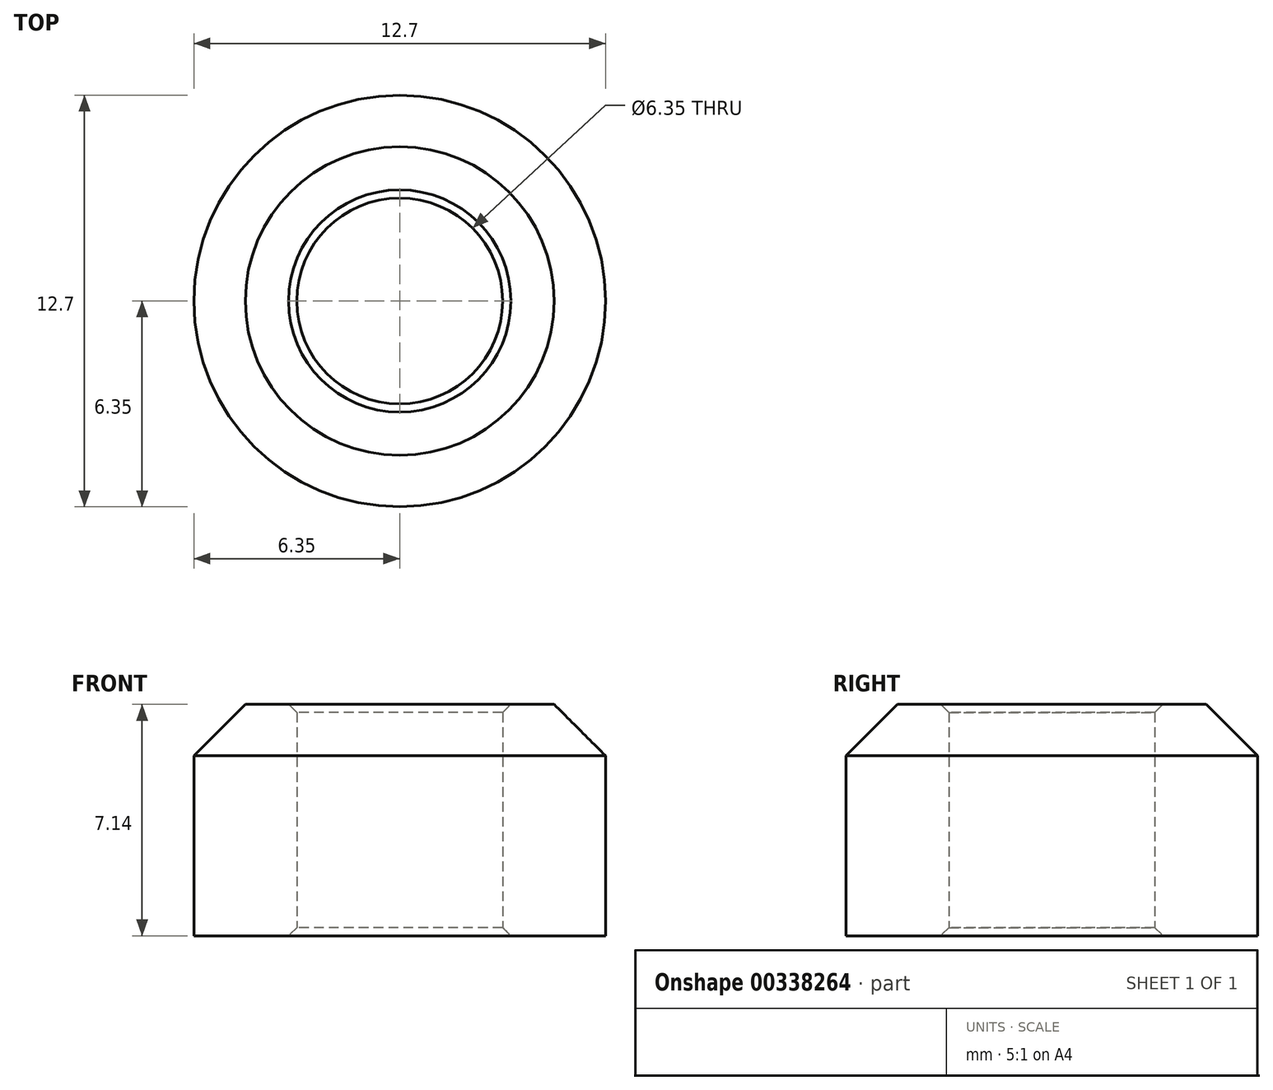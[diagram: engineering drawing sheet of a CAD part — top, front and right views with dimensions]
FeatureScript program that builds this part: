
annotation { "Feature Type Name" : "Feature", "Feature Type Description" : "" }
export const myFeature = defineFeature(function(context is Context, id is Id, definition is map)
    precondition{}
    {
        {
            var Q0;
            Q0=qCreatedBy(makeId("Top.planeOp"),FACE);
            var sketch = newSketch(context, id + "F0", { "sketchPlane" : qUnion([Q0])});
            skCircle(sketch, "E0", {"center": v(0, 0) * mm, "radius": 6.35 * mm});
            skCircle(sketch, "E1", {"center": v(0, 0) * mm, "radius": 3.18 * mm});
            skSolve(sketch);
        }
        {
            var Q0;
            Q0=qSketchRegion(id+"F0",true);
            extrude(context, id + "F1", {"entities" : qUnion([Q0]), "depth" : 7.14 * mm});
        }
        {
            var Q0;
            Q0=makeQuery(id+"F1.opExtrude","CAP_EDGE",EDGE,{"disambiguationData":[OSD([sQuery(id+"F0.wireOp",EDGE,"E0")])],"isStart":false});
            chamfer(context, id + "F2", {"entities" : qUnion([Q0]), "width" : 1.59 * mm, "tangentPropagation" : true});
        }
        {
            var Q0;
            Q0=makeQuery(id+"F1.opExtrude","CAP_EDGE",EDGE,{"disambiguationData":[OSD([sQuery(id+"F0.wireOp",EDGE,"E1")])],"isStart":false});
            var Q1;
            Q1=makeQuery(id+"F1.opExtrude","CAP_EDGE",EDGE,{"disambiguationData":[OSD([sQuery(id+"F0.wireOp",EDGE,"E1")])],"isStart":true});
            chamfer(context, id + "F3", {"entities" : qUnion([Q0, Q1]), "width" : 0.25 * mm, "tangentPropagation" : true});
        }
    });
